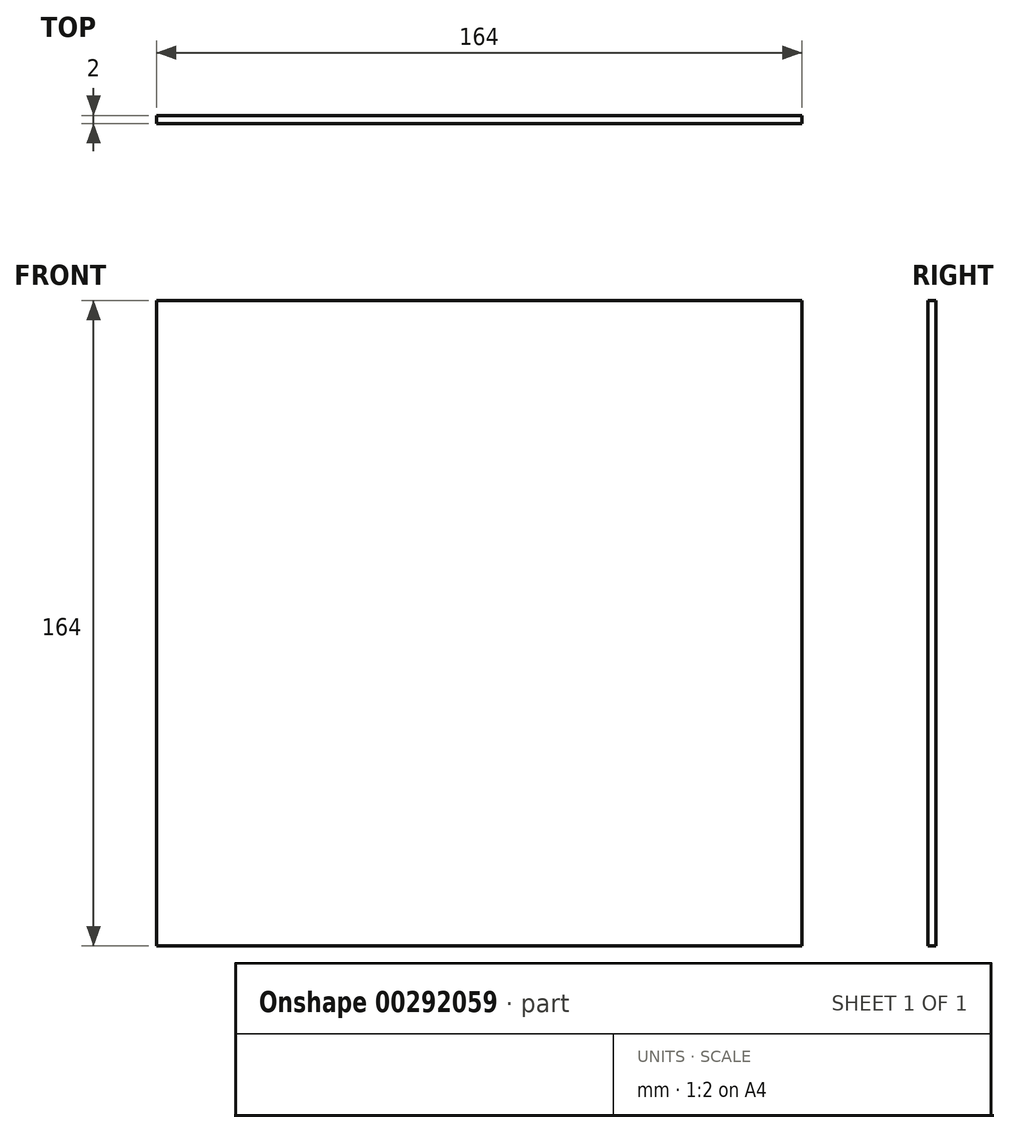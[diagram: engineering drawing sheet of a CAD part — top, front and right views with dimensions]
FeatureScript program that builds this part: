
annotation { "Feature Type Name" : "Feature", "Feature Type Description" : "" }
export const myFeature = defineFeature(function(context is Context, id is Id, definition is map)
    precondition{}
    {
        {
            var Q0;
            Q0=qCreatedBy(makeId("Front.planeOp"),FACE);
            var sketch = newSketch(context, id + "F0", { "sketchPlane" : qUnion([Q0])});
            skLineSegment(sketch, "E0.bottom", {"start": v(82, -82) * mm, "end": v(-82, -82) * mm});
            skLineSegment(sketch, "E0.top", {"start": v(82, 82) * mm, "end": v(-82, 82) * mm});
            skLineSegment(sketch, "E0.left", {"start": v(82, -82) * mm, "end": v(82, 82) * mm});
            skLineSegment(sketch, "E0.right", {"start": v(-82, -82) * mm, "end": v(-82, 82) * mm});
            skPoint(sketch, "E0.middle", {"position": v(0, 0) * mm});
            skSolve(sketch);
        }
        {
            var Q0;
            Q0 = qSketchRegion(id + "F0", true);
            extrude(context, id + "F1", {"entities" : qUnion([Q0]), "depth" : 2 * mm});
        }
    });
